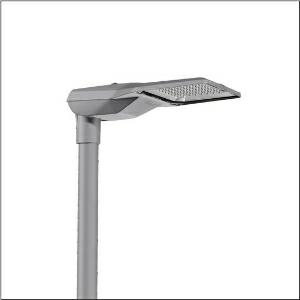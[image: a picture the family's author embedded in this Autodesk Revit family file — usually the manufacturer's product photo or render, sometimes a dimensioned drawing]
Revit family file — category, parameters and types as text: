
# Revit family: streetlight_sl_21_midi___p0_8ab_5xe3r33s08lb_9dc6
name_source: partatom
category: Lighting Fixtures
units: mm (PartAtom-declared; Revit-internal decimal feet)

## family parameters
Cut with Voids When Loaded = No
Host = Face
Light Source = No
Part Type = Normal
Room Calculation Point = No
Round Connector Dimension = Use Diameter
Shared = No

## types (1)
- --- (1 x LED, 12450 lm, 99.6 W, 3000K)
    Apparent Load = 100 VA
    CIE Flux Codes = 36 71 98 100 100
    Color Rendering = 70
    Color Temperature = 3000K
    Default Elevation = 1800 mm
    Description = Streetlight SL 21 midi, mast luminaire, primary light control with lens, of PMMA, primary optical cover: cover, of toughened safety glass, transparent, light distribution: P0.8aB, light emission: direct distribution, primary light characteristic: asymmetric, installation type: post-top, side-entry, LED, High Power LED, rated luminous flux: 12.450lm, luminous efficacy: 125lm/W, light colour: 730, colour temperature: 3000K, control gear: D4i, control: pre-setting: logarithmic dimming characteristic, flexible luminous flux parameterisation, time-dependent luminous flux control, constant luminous flux control, overheat protection, mains connection: 230..240V, AC, 50/60Hz, start of lifetime: 100W, end of service life: 102W, reduction: 46W, luminaire housing, of diecast aluminium, powder-coated, Siteco® metallic grey (DB 702S), corrosivity category C5 mid according to DIN EN ISO 12944, multi-level sealing system, sealing non-destructively replaceable, inclination adjustable: 0°, 5°, 10°, 15°, please order mast flange separately, length: 644mm, width: 335mm, height: 110mm, mast flange for spigot size: 42mm (side-entry): 5XC10008XM4, 60/48mm (side-entry/post-top): 5XC10108XM2, 76/60mm (side-entry/post-top): 5XC10108XM1, mounting height: 4..8m, Smart Interface above, protection rating (complete): IP66, insulation class (complete): insulation class II (safety insulation), certification: CE, ENEC, ENEC+, VDE, impact resistance: IK10, permissible operating ambient temperature for outdoor applications: -40..+50°C, standard-compliant lighting for roads and squares, packaging unit: 1 piece

Light Distribution: P0.8aB
    Height = 111 mm
    Lamp = 1 x LED
    Lamp Light Flux = 12450 lm
    Lamp Power = 99.6 W
    Lamp count = 1
    Length = 644 mm
    Luminous efficacy = 125 lm/W
    Manufacturer = Siteco
    ModVariant = No
    Model = 5XE3R33S08LB
    Number of Poles = 1
    OnlyDefault = Yes
    Power Factor = 1
    Product Name = Streetlight SL 21 midi | P0.8aB
    Product group = mast luminaire | pylon top
    ProductGroupID = 6100
    Protection Class = Protection class II
    Protection Degree = IP 66
    RLX_Detail_Level = 1
    RLX_Emergency_Light_Flux = 0 lm
    RLX_Emergency_Type = 0
    RLX_Emergency_Type_DB = No
    RlxData = <blob elided: 26465 chars, md5=7dcc1e10>
    Socket = socket
    Standby Power = 0 W
    System Light Flux = 12450 lm
    System Power = 100 W
    Type Comments = factory setting: luminous flux: 100 % | dim-lin: 254 | 1020 mA
    Type Image = l_1004302.jpg
    URL = http://relux.com
    VarID = @adj_013547
    Voltage = 0 V
    Weight = 0.00 kg
    Width = 336 mm

## geometry (parser evidence)
native form markers: Blend x4, Sweep x12
no freeform markers — native parametric forms only
